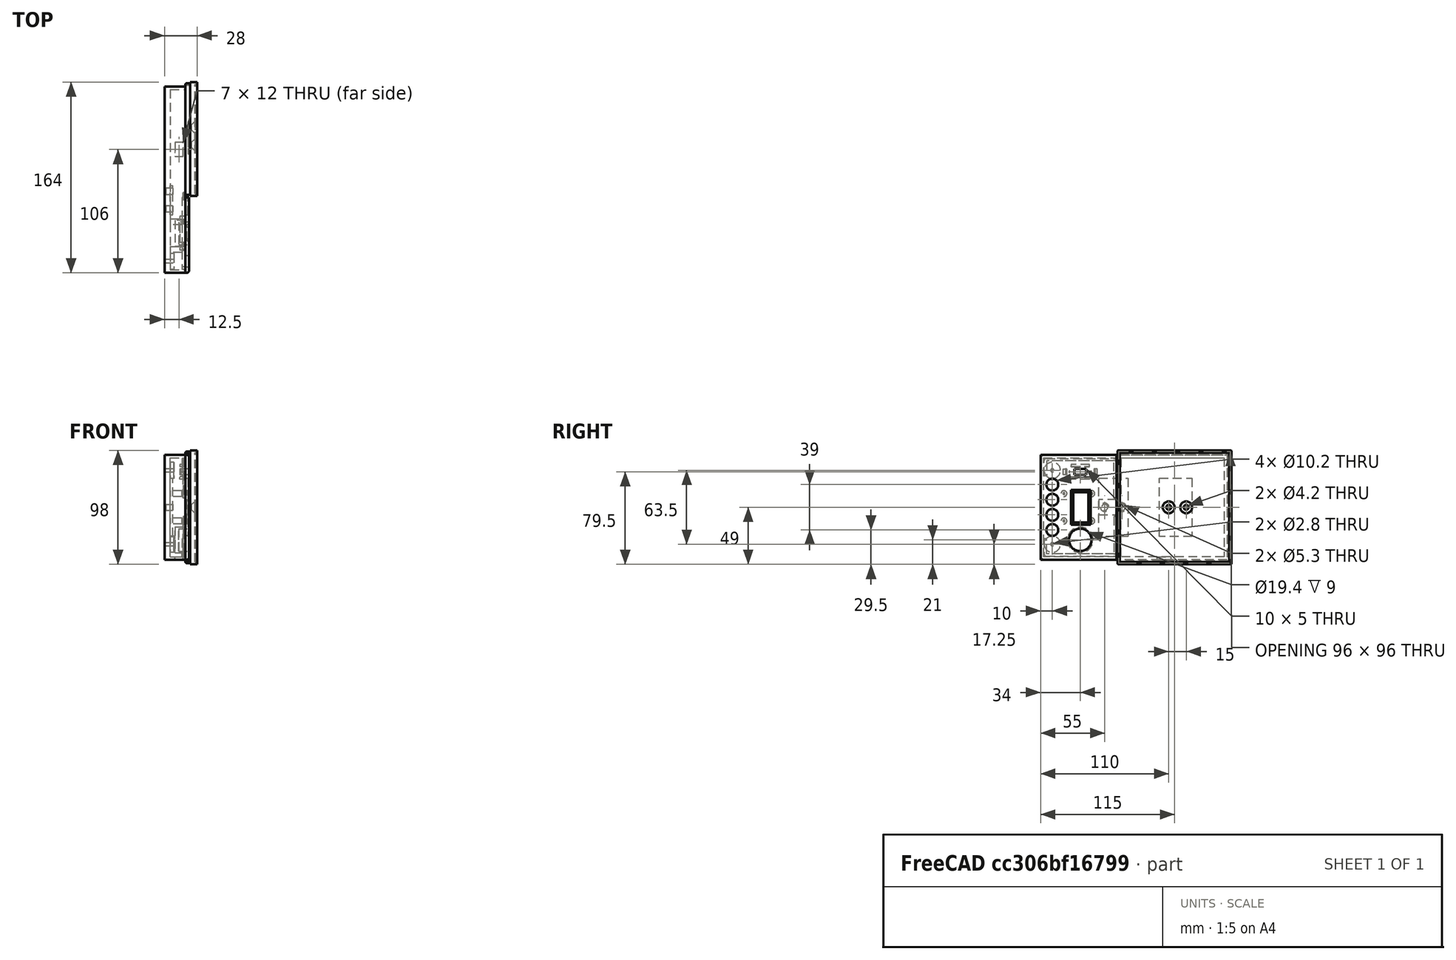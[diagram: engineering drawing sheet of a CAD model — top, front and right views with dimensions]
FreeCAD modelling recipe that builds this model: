
FCSTD DOCUMENT  (FreeCAD 0.19R24291 (Git))
Label: Waagenplattform
License: All rights reserved
LicenseURL: http://en.wikipedia.org/wiki/All_rights_reserved
objects: Sketcher::SketchObject×24, PartDesign::Fillet×18, PartDesign::Pad×16, PartDesign::Chamfer×16, PartDesign::Pocket×7, PartDesign::Body×3, Mesh::Feature×1
note: 141 computed .brp shape members not serialized (recipe doc carries the construction recipe); baked Part::Feature solids carry a one-line shape summary decoded from their .brp

FEATURE [Sketcher::SketchObject] Sketch
  FullyConstrained = true
  MapMode = 5
  Placement = pos=(0,0,0) rot=(0.57735,0.57735,0.57735;2.0944rad)
  Support = -> [YZ_Plane]
  sketch-geometry (4):
    g0: LineSegment StartX=0 StartY=45 StartZ=0 EndX=160 EndY=45 EndZ=0
    g1: LineSegment StartX=160 StartY=45 StartZ=0 EndX=160 EndY=-45 EndZ=0
    g2: LineSegment StartX=160 StartY=-45 StartZ=0 EndX=0 EndY=-45 EndZ=0
    g3: LineSegment StartX=0 StartY=-45 StartZ=0 EndX=0 EndY=45 EndZ=0
  constraints (12):
    c: Coincident(g0,g1)
    c: Coincident(g1,g2)
    c: Coincident(g2,g3)
    c: Coincident(g3,g0)
    c: Horizontal(g0)
    c: Horizontal(g2)
    c: Vertical(g1)
    c: Vertical(g3)
    c: DistanceX(g0,g0) = 160
    c: DistanceY(g3,g3) = 90
    c: PointOnObject(g-1,g3)
    c: Distance(g-1,g0) = 45
FEATURE [PartDesign::Pad] Pad
  Direction = (1,1,1)
  Length = 5
  Length2 = 100
  Placement = pos=(0,0,0) rot=(0.57735,0.57735,0.57735;2.0944rad)
  Profile = -> Sketch
  Refine = true
  Type = 0
FEATURE [Sketcher::SketchObject] Sketch001
  FullyConstrained = true
  MapMode = 5
  Placement = pos=(5,-1.1e-15,1.1e-15) rot=(0.57735,0.57735,0.57735;2.0944rad)
  Support = -> [Pad]
  sketch-geometry (2):
    g0: Circle CenterX=10 CenterY=31.75 CenterZ=0 NormalX=0 NormalY=0 NormalZ=1 AngleXU=0 Radius=7
    g1: Circle CenterX=10 CenterY=-31.75 CenterZ=0 NormalX=0 NormalY=0 NormalZ=1 AngleXU=0 Radius=7
  constraints (5):
    c: Distance(g0,g1) = 63.5
    c: Symmetric(g0,g1,g-1)
    c: DistanceX(g-1,g0) = 10
    c: Radius(g0) = 7
    c: Radius(g1) = 7
FEATURE [PartDesign::Pad] Pad001
  BaseFeature = -> Pad
  Direction = (1,1,1)
  Length = 3
  Length2 = 100
  Placement = pos=(0,0,0) rot=(0.57735,0.57735,0.57735;2.0944rad)
  Profile = -> Sketch001
  Refine = true
  Type = 0
FEATURE [Sketcher::SketchObject] Sketch002
  FullyConstrained = true
  MapMode = 5
  Placement = pos=(5,-1.1e-15,1.1e-15) rot=(0.57735,0.57735,0.57735;2.0944rad)
  Support = -> [Pad001]
  sketch-geometry (4):
    g0: Circle CenterX=20 CenterY=11.75 CenterZ=0 NormalX=0 NormalY=0 NormalZ=1 AngleXU=0 Radius=2.5
    g1: Circle CenterX=44 CenterY=11.75 CenterZ=0 NormalX=0 NormalY=0 NormalZ=1 AngleXU=0 Radius=2.5
    g2: Circle CenterX=20 CenterY=-11.75 CenterZ=0 NormalX=0 NormalY=0 NormalZ=1 AngleXU=0 Radius=2.5
    g3: Circle CenterX=44 CenterY=-11.75 CenterZ=0 NormalX=0 NormalY=0 NormalZ=1 AngleXU=0 Radius=2.5
  constraints (11):
    c: DistanceX(g2,g3) = 24
    c: DistanceY(g3,g1) = 23.5
    c: Vertical(g0,g2)
    c: Horizontal(g0,g1)
    c: Horizontal(g2,g3)
    c: Radius(g0) = 2.5
    c: Radius(g1) = 2.5
    c: Radius(g3) = 2.5
    c: Radius(g2) = 2.5
    c: Symmetric(g1,g3,g-1)
    c: DistanceX(g-1,g0) = 20
FEATURE [PartDesign::Pad] Pad002
  BaseFeature = -> Pad001
  Direction = (1,1,1)
  Length = 10
  Length2 = 100
  Placement = pos=(0,0,0) rot=(0.57735,0.57735,0.57735;2.0944rad)
  Profile = -> Sketch002
  Refine = true
  Type = 0
FEATURE [Sketcher::SketchObject] Sketch003
  ExternalGeometry = -> [Pad002]
  FullyConstrained = true
  MapMode = 5
  Placement = pos=(15,-8.8e-15,9.3e-15) rot=(0.57735,0.57735,0.57735;2.0944rad)
  Support = -> [Pad002]
  sketch-geometry (4):
    g0: Circle CenterX=44 CenterY=11.75 CenterZ=0 NormalX=0 NormalY=0 NormalZ=1 AngleXU=0 Radius=0.8
    g1: Circle CenterX=20 CenterY=11.75 CenterZ=0 NormalX=0 NormalY=0 NormalZ=1 AngleXU=0 Radius=0.8
    g2: Circle CenterX=20 CenterY=-11.75 CenterZ=0 NormalX=0 NormalY=0 NormalZ=1 AngleXU=0 Radius=0.8
    g3: Circle CenterX=44 CenterY=-11.75 CenterZ=0 NormalX=0 NormalY=0 NormalZ=1 AngleXU=0 Radius=0.8
  constraints (8):
    c: Coincident(g0,g-3)
    c: Radius(g0) = 0.8
    c: Coincident(g1,g-4)
    c: Coincident(g2,g-5)
    c: Coincident(g3,g-6)
    c: Radius(g1) = 0.8
    c: Radius(g2) = 0.8
    c: Radius(g3) = 0.8
FEATURE [PartDesign::Pad] Pad003
  BaseFeature = -> Pad002
  Direction = (1,1,1)
  Length = 2.5
  Length2 = 100
  Placement = pos=(0,0,0) rot=(0.57735,0.57735,0.57735;2.0944rad)
  Profile = -> Sketch003
  Refine = true
  Type = 0
FEATURE [Sketcher::SketchObject] Sketch004
  ExternalGeometry = -> [Pad003]
  FullyConstrained = true
  MapMode = 5
  Placement = pos=(8,-4.1e-15,3.5e-15) rot=(0.57735,0.57735,0.57735;2.0944rad)
  Support = -> [Pad003]
  sketch-geometry (2):
    g0: Circle CenterX=10 CenterY=31.75 CenterZ=0 NormalX=0 NormalY=0 NormalZ=1 AngleXU=0 Radius=1.4
    g1: Circle CenterX=10 CenterY=-31.75 CenterZ=0 NormalX=0 NormalY=0 NormalZ=1 AngleXU=0 Radius=1.4
  constraints (4):
    c: Coincident(g0,g-3)
    c: Coincident(g1,g-4)
    c: Radius(g0) = 1.4
    c: Radius(g1) = 1.4
FEATURE [PartDesign::Pocket] Pocket
  BaseFeature = -> Pad003
  Length = 8
  Length2 = 100
  Placement = pos=(0,0,0) rot=(0.57735,0.57735,0.57735;2.0944rad)
  Profile = -> Sketch004
  Refine = true
  Type = 0
FEATURE [Sketcher::SketchObject] Sketch005
  FullyConstrained = true
  MapMode = 5
  Placement = pos=(5,-1.1e-15,1.1e-15) rot=(0.57735,0.57735,0.57735;2.0944rad)
  Support = -> [Pocket]
  sketch-geometry (4):
    g0: LineSegment StartX=50 StartY=25 StartZ=0 EndX=75 EndY=25 EndZ=0
    g1: LineSegment StartX=75 StartY=25 StartZ=0 EndX=75 EndY=-25 EndZ=0
    g2: LineSegment StartX=75 StartY=-25 StartZ=0 EndX=50 EndY=-25 EndZ=0
    g3: LineSegment StartX=50 StartY=-25 StartZ=0 EndX=50 EndY=25 EndZ=0
  constraints (11):
    c: Coincident(g0,g1)
    c: Coincident(g1,g2)
    c: Coincident(g2,g3)
    c: Coincident(g3,g0)
    c: Horizontal(g0)
    c: Horizontal(g2)
    c: Vertical(g1)
    c: DistanceX(g0,g0) = 25
    c: DistanceY(g3,g3) = 50
    c: Symmetric(g0,g2,g-1)
    c: DistanceX(g-1,g0) = 50
FEATURE [PartDesign::Pad] Pad004
  BaseFeature = -> Pocket
  Direction = (1,1,1)
  Length = 2
  Length2 = 100
  Placement = pos=(0,0,0) rot=(0.57735,0.57735,0.57735;2.0944rad)
  Profile = -> Sketch005
  Refine = true
  Type = 0
FEATURE [Sketcher::SketchObject] Sketch006
  ExternalGeometry = -> [Pad004]
  FullyConstrained = true
  MapMode = 5
  Placement = pos=(7,-9.2e-15,6.2e-15) rot=(0.57735,0.57735,0.57735;2.0944rad)
  Support = -> [Pad004]
  sketch-geometry (2):
    g0: Circle CenterX=55 CenterY=0 CenterZ=0 NormalX=0 NormalY=0 NormalZ=1 AngleXU=0 Radius=2.65
    g1: Circle CenterX=70 CenterY=0 CenterZ=0 NormalX=0 NormalY=0 NormalZ=1 AngleXU=0 Radius=2.65
  constraints (6):
    c: PointOnObject(g0,g-1)
    c: PointOnObject(g1,g-1)
    c: DistanceX(g0,g1) = 15
    c: Distance(g0,g-3) = 5
    c: Radius(g0) = 2.65
    c: Radius(g1) = 2.65
FEATURE [PartDesign::Pocket] Pocket001
  BaseFeature = -> Pad004
  Length = 7
  Length2 = 100
  Placement = pos=(0,0,0) rot=(0.57735,0.57735,0.57735;2.0944rad)
  Profile = -> Sketch006
  Refine = true
  Type = 0
FEATURE [PartDesign::Chamfer] Chamfer
  Angle = 45
  Base = -> Pocket001 [Edge13]
  BaseFeature = -> Pocket001
  ChamferType = 0
  FlipDirection = false
  Placement = pos=(0,0,0) rot=(0.57735,0.57735,0.57735;2.0944rad)
  Refine = true
  Size = 1
  Size2 = 1
  SupportTransform = false
FEATURE [PartDesign::Chamfer] Chamfer001
  Angle = 45
  Base = -> Chamfer [Edge6]
  BaseFeature = -> Chamfer
  ChamferType = 0
  FlipDirection = false
  Placement = pos=(0,0,0) rot=(0.57735,0.57735,0.57735;2.0944rad)
  Refine = true
  Size = 1
  Size2 = 1
  SupportTransform = false
FEATURE [Sketcher::SketchObject] Sketch007
  ExternalGeometry = -> [Chamfer001]
  FullyConstrained = true
  MapMode = 5
  Placement = pos=(5,-1.1e-15,1.1e-15) rot=(0.57735,0.57735,0.57735;2.0944rad)
  Support = -> [Chamfer001]
  sketch-geometry (8):
    g0: LineSegment StartX=4e-14 StartY=45 StartZ=0 EndX=160 EndY=45 EndZ=0
    g1: LineSegment StartX=160 StartY=45 StartZ=0 EndX=160 EndY=-45 EndZ=0
    g2: LineSegment StartX=160 StartY=-45 StartZ=0 EndX=2.84e-14 EndY=-45 EndZ=0
    g3: LineSegment StartX=4e-14 StartY=-45 StartZ=0 EndX=4e-14 EndY=45 EndZ=0
    g4: LineSegment StartX=2.5 StartY=42.5 StartZ=0 EndX=157.5 EndY=42.5 EndZ=0
    g5: LineSegment StartX=157.5 StartY=42.5 StartZ=0 EndX=157.5 EndY=-42.5 EndZ=0
    g6: LineSegment StartX=157.5 StartY=-42.5 StartZ=0 EndX=2.5 EndY=-42.5 EndZ=0
    g7: LineSegment StartX=2.5 StartY=-42.5 StartZ=0 EndX=2.5 EndY=42.5 EndZ=0
  constraints (22):
    c: Coincident(g0,g1)
    c: Coincident(g1,g2)
    c: Coincident(g2,g3)
    c: Coincident(g3,g0)
    c: Horizontal(g0)
    c: Horizontal(g2)
    c: Vertical(g1)
    c: Vertical(g3)
    c: Coincident(g0,g-6)
    c: Coincident(g1,g-5)
    c: Coincident(g4,g5)
    c: Coincident(g5,g6)
    c: Coincident(g6,g7)
    c: Coincident(g7,g4)
    c: Horizontal(g4)
    c: Horizontal(g6)
    c: Vertical(g5)
    c: Vertical(g7)
    c: Distance(g4,g0) = 2.5
    c: Distance(g4,g1) = 2.5
    c: Distance(g5,g2) = 2.5
    c: Distance(g6,g3) = 2.5
FEATURE [PartDesign::Pad] Pad005
  BaseFeature = -> Chamfer001
  Direction = (1,1,1)
  Length = 13
  Length2 = 100
  Placement = pos=(0,0,0) rot=(0.57735,0.57735,0.57735;2.0944rad)
  Profile = -> Sketch007
  Refine = true
  Type = 0
FEATURE [Sketcher::SketchObject] Sketch008
  ExternalGeometry = -> [Pad005]
  FullyConstrained = true
  MapMode = 5
  Placement = pos=(-1.332e-13,-1.93e-14,-45) rot=(0.707107,0.707107,0;3.14159rad)
  Support = -> [Pad005]
  sketch-geometry (4):
    g0: LineSegment StartX=100 StartY=16 StartZ=0 EndX=112 EndY=16 EndZ=0
    g1: LineSegment StartX=112 StartY=16 StartZ=0 EndX=112 EndY=9 EndZ=0
    g2: LineSegment StartX=112 StartY=9 StartZ=0 EndX=100 EndY=9 EndZ=0
    g3: LineSegment StartX=100 StartY=9 StartZ=0 EndX=100 EndY=16 EndZ=0
  constraints (12):
    c: Coincident(g0,g1)
    c: Coincident(g1,g2)
    c: Coincident(g2,g3)
    c: Coincident(g3,g0)
    c: Horizontal(g0)
    c: Horizontal(g2)
    c: Vertical(g1)
    c: Vertical(g3)
    c: DistanceX(g0,g0) = 12
    c: DistanceY(g1,g1) = 7
    c: Distance(g1,g-3) = 9
    c: Distance(g2,g-4) = 100
FEATURE [PartDesign::Pocket] Pocket002
  BaseFeature = -> Pad005
  Length = 5
  Length2 = 100
  Placement = pos=(0,0,0) rot=(0.57735,0.57735,0.57735;2.0944rad)
  Profile = -> Sketch008
  Refine = true
  Type = 0
FEATURE [PartDesign::Body] Body
  Group = -> [Sketch,Pad,Sketch001,Pad001,Sketch002,Pad002,Sketch003,Pad003,Sketch004,Pocket,Sketch005,Pad004,Sketch006,Pocket001,Chamfer,Chamfer001,Sketch007,Pad005,Sketch008,Pocket002]
  Origin = -> Origin
  Tip = -> Pocket002
FEATURE [Sketcher::SketchObject] Sketch009
  AttachmentOffset = pos=(0,0,22) rot=(0,0,1;0rad)
  FullyConstrained = true
  MapMode = 5
  Placement = pos=(22,-4.9e-15,4.9e-15) rot=(0.57735,0.57735,0.57735;2.0944rad)
  Support = -> [YZ_Plane001]
  sketch-geometry (4):
    g0: LineSegment StartX=66 StartY=49 StartZ=0 EndX=164 EndY=49 EndZ=0
    g1: LineSegment StartX=164 StartY=49 StartZ=0 EndX=164 EndY=-49 EndZ=0
    g2: LineSegment StartX=164 StartY=-49 StartZ=0 EndX=66 EndY=-49 EndZ=0
    g3: LineSegment StartX=66 StartY=-49 StartZ=0 EndX=66 EndY=49 EndZ=0
  constraints (11):
    c: Coincident(g0,g1)
    c: Coincident(g1,g2)
    c: Coincident(g2,g3)
    c: Coincident(g3,g0)
    c: Horizontal(g0)
    c: Horizontal(g2)
    c: Vertical(g3)
    c: DistanceY(g1,g1) = 98
    c: DistanceX(g0,g0) = 98
    c: Symmetric(g0,g1,g-1)
    c: DistanceX(g-1,g0) = 66
FEATURE [PartDesign::Pad] Pad006
  Direction = (1,1,1)
  Length = 4
  Length2 = 100
  Placement = pos=(0,0,0) rot=(0.57735,0.57735,0.57735;2.0944rad)
  Profile = -> Sketch009
  Refine = true
  Type = 0
FEATURE [Sketcher::SketchObject] Sketch010
  ExternalGeometry = -> [Pad006]
  FullyConstrained = true
  MapMode = 5
  Placement = pos=(22,-4.8e-15,4.8e-15) rot=(0.57735,0.57735,-0.57735;4.18879rad)
  Support = -> [Pad006]
  sketch-geometry (4):
    g0: LineSegment StartX=130 StartY=25 StartZ=0 EndX=102 EndY=25 EndZ=0
    g1: LineSegment StartX=102 StartY=25 StartZ=0 EndX=102 EndY=-25 EndZ=0
    g2: LineSegment StartX=102 StartY=-25 StartZ=0 EndX=130 EndY=-25 EndZ=0
    g3: LineSegment StartX=130 StartY=-25 StartZ=0 EndX=130 EndY=25 EndZ=0
  constraints (11):
    c: Coincident(g0,g1)
    c: Coincident(g1,g2)
    c: Coincident(g2,g3)
    c: Coincident(g3,g0)
    c: Horizontal(g0)
    c: Horizontal(g2)
    c: Vertical(g3)
    c: DistanceX(g0,g0) = 28
    c: DistanceY(g3,g3) = 50
    c: Symmetric(g0,g1,g-1)
    c: Distance(g0,g-3) = 34
FEATURE [PartDesign::Pad] Pad007
  BaseFeature = -> Pad006
  Direction = (1,1,1)
  Length = 2
  Length2 = 100
  Placement = pos=(0,0,0) rot=(0.57735,0.57735,0.57735;2.0944rad)
  Profile = -> Sketch010
  Refine = true
  Type = 0
FEATURE [Sketcher::SketchObject] Sketch011
  ExternalGeometry = -> [Pad007]
  FullyConstrained = true
  MapMode = 5
  Placement = pos=(20,-7.6e-15,5.6e-15) rot=(-0.57735,-0.57735,0.57735;2.0944rad)
  Support = -> [Pad007]
  sketch-geometry (2):
    g0: Circle CenterX=125 CenterY=0 CenterZ=0 NormalX=0 NormalY=0 NormalZ=1 AngleXU=0 Radius=2.1
    g1: Circle CenterX=110 CenterY=0 CenterZ=0 NormalX=0 NormalY=0 NormalZ=1 AngleXU=0 Radius=2.1
  constraints (6):
    c: PointOnObject(g0,g-1)
    c: PointOnObject(g1,g-1)
    c: Radius(g0) = 2.1
    c: Radius(g1) = 2.1
    c: DistanceX(g1,g0) = 15
    c: Distance(g0,g-3) = 5
FEATURE [PartDesign::Pocket] Pocket003
  BaseFeature = -> Pad007
  Length = 6
  Length2 = 100
  Placement = pos=(0,0,0) rot=(0.57735,0.57735,0.57735;2.0944rad)
  Profile = -> Sketch011
  Refine = true
  Type = 0
FEATURE [Sketcher::SketchObject] Sketch012
  ExternalGeometry = -> [Pocket003]
  FullyConstrained = true
  MapMode = 5
  Placement = pos=(22,-4.8e-15,4.8e-15) rot=(0.57735,0.57735,-0.57735;4.18879rad)
  Support = -> [Pocket003]
  sketch-geometry (8):
    g0: LineSegment StartX=163 StartY=48 StartZ=0 EndX=163 EndY=-48 EndZ=0
    g1: LineSegment StartX=163 StartY=-48 StartZ=0 EndX=67 EndY=-48 EndZ=0
    g2: LineSegment StartX=67 StartY=-46 StartZ=0 EndX=161 EndY=-46 EndZ=0
    g3: LineSegment StartX=161 StartY=-46 StartZ=0 EndX=161 EndY=46 EndZ=0
    g4: LineSegment StartX=67 StartY=-46 StartZ=0 EndX=67 EndY=-48 EndZ=0
    g5: LineSegment StartX=161 StartY=46 StartZ=0 EndX=67 EndY=46 EndZ=0
    g6: LineSegment StartX=67 StartY=46 StartZ=0 EndX=67 EndY=48 EndZ=0
    g7: LineSegment StartX=67 StartY=48 StartZ=0 EndX=163 EndY=48 EndZ=0
  constraints (23):
    c: Vertical(g0)
    c: Coincident(g0,g1)
    c: Horizontal(g1)
    c: Horizontal(g2)
    c: Coincident(g2,g3)
    c: Vertical(g3)
    c: DistanceY(g1,g2) = 2
    c: DistanceX(g3,g0) = 2
    c: Coincident(g4,g2)
    c: Coincident(g4,g1)
    c: Coincident(g5,g3)
    c: Horizontal(g5)
    c: Coincident(g6,g5)
    c: Coincident(g7,g6)
    c: Coincident(g7,g0)
    c: Horizontal(g7)
    c: Vertical(g6)
    c: Vertical(g4)
    c: DistanceY(g5,g6) = 2
    c: DistanceY(g2,g5) = 92
    c: Symmetric(g5,g2,g-1)
    c: Distance(g-7,g3) = 31
    c: DistanceX(g7,g7) = 96
FEATURE [PartDesign::Pad] Pad008
  BaseFeature = -> Pocket003
  Direction = (1,1,1)
  Length = 4
  Length2 = 100
  Placement = pos=(0,0,0) rot=(0.57735,0.57735,0.57735;2.0944rad)
  Profile = -> Sketch012
  Refine = true
  Type = 0
FEATURE [Sketcher::SketchObject] Sketch013
  ExternalGeometry = -> [Pad008]
  FullyConstrained = true
  MapMode = 5
  Placement = pos=(26,-5.7e-15,5.7e-15) rot=(0.57735,0.57735,0.57735;2.0944rad)
  Support = -> [Pad008]
  sketch-geometry (8):
    g0: LineSegment StartX=66 StartY=49 StartZ=0 EndX=164 EndY=49 EndZ=0
    g1: LineSegment StartX=164 StartY=49 StartZ=0 EndX=164 EndY=-49 EndZ=0
    g2: LineSegment StartX=164 StartY=-49 StartZ=0 EndX=66 EndY=-49 EndZ=0
    g3: LineSegment StartX=66 StartY=-49 StartZ=0 EndX=66 EndY=49 EndZ=0
    g4: LineSegment StartX=68 StartY=47 StartZ=0 EndX=162 EndY=47 EndZ=0
    g5: LineSegment StartX=162 StartY=47 StartZ=0 EndX=162 EndY=-47 EndZ=0
    g6: LineSegment StartX=162 StartY=-47 StartZ=0 EndX=68 EndY=-47 EndZ=0
    g7: LineSegment StartX=68 StartY=-47 StartZ=0 EndX=68 EndY=47 EndZ=0
  constraints (22):
    c: Coincident(g0,g1)
    c: Coincident(g1,g2)
    c: Coincident(g2,g3)
    c: Coincident(g3,g0)
    c: Horizontal(g0)
    c: Horizontal(g2)
    c: Vertical(g1)
    c: Vertical(g3)
    c: Coincident(g0,g-4)
    c: Coincident(g1,g-6)
    c: Coincident(g4,g5)
    c: Coincident(g5,g6)
    c: Coincident(g6,g7)
    c: Coincident(g7,g4)
    c: Horizontal(g4)
    c: Horizontal(g6)
    c: Vertical(g5)
    c: Vertical(g7)
    c: DistanceY(g4,g0) = 2
    c: DistanceY(g2,g6) = 2
    c: DistanceX(g0,g4) = 2
    c: DistanceX(g4,g0) = 2
FEATURE [PartDesign::Pad] Pad009
  BaseFeature = -> Pad008
  Direction = (1,1,1)
  Length = 2
  Length2 = 100
  Placement = pos=(0,0,0) rot=(0.57735,0.57735,0.57735;2.0944rad)
  Profile = -> Sketch013
  Refine = true
  Type = 0
FEATURE [PartDesign::Chamfer] Chamfer002
  Angle = 45
  Base = -> Pad009 [Edge18]
  BaseFeature = -> Pad009
  ChamferType = 0
  FlipDirection = false
  Placement = pos=(0,0,0) rot=(0.57735,0.57735,0.57735;2.0944rad)
  Refine = true
  Size = 3
  Size2 = 1
  SupportTransform = false
FEATURE [PartDesign::Chamfer] Chamfer003
  Angle = 45
  Base = -> Chamfer002 [Edge6]
  BaseFeature = -> Chamfer002
  ChamferType = 0
  FlipDirection = false
  Placement = pos=(0,0,0) rot=(0.57735,0.57735,0.57735;2.0944rad)
  Refine = true
  Size = 3
  Size2 = 1
  SupportTransform = false
FEATURE [PartDesign::Chamfer] Chamfer004
  Angle = 45
  Base = -> Chamfer003 [Edge15]
  BaseFeature = -> Chamfer003
  ChamferType = 0
  FlipDirection = false
  Placement = pos=(0,0,0) rot=(0.57735,0.57735,0.57735;2.0944rad)
  Refine = true
  Size = 1
  Size2 = 1
  SupportTransform = false
FEATURE [PartDesign::Chamfer] Chamfer005
  Angle = 45
  Base = -> Chamfer004 [Edge17]
  BaseFeature = -> Chamfer004
  ChamferType = 0
  FlipDirection = false
  Placement = pos=(0,0,0) rot=(0.57735,0.57735,0.57735;2.0944rad)
  Refine = true
  Size = 1
  Size2 = 1
  SupportTransform = false
FEATURE [PartDesign::Chamfer] Chamfer006
  Angle = 45
  Base = -> Chamfer005 [Edge5]
  BaseFeature = -> Chamfer005
  ChamferType = 0
  FlipDirection = false
  Placement = pos=(0,0,0) rot=(0.57735,0.57735,0.57735;2.0944rad)
  Refine = true
  Size = 1
  Size2 = 1
  SupportTransform = false
FEATURE [PartDesign::Chamfer] Chamfer007
  Angle = 45
  Base = -> Chamfer006 [Edge2]
  BaseFeature = -> Chamfer006
  ChamferType = 0
  FlipDirection = false
  Placement = pos=(0,0,0) rot=(0.57735,0.57735,0.57735;2.0944rad)
  Refine = true
  Size = 1
  Size2 = 1
  SupportTransform = false
FEATURE [PartDesign::Fillet] Fillet
  Base = -> Chamfer007 [Edge19]
  BaseFeature = -> Chamfer007
  Placement = pos=(0,0,0) rot=(0.57735,0.57735,0.57735;2.0944rad)
  Radius = 1
  Refine = true
  SupportTransform = false
FEATURE [PartDesign::Fillet] Fillet001
  Base = -> Fillet [Edge17]
  BaseFeature = -> Fillet
  Placement = pos=(0,0,0) rot=(0.57735,0.57735,0.57735;2.0944rad)
  Radius = 1
  Refine = true
  SupportTransform = false
FEATURE [PartDesign::Fillet] Fillet002
  Base = -> Fillet001 [Edge18]
  BaseFeature = -> Fillet001
  Placement = pos=(0,0,0) rot=(0.57735,0.57735,0.57735;2.0944rad)
  Radius = 1
  Refine = true
  SupportTransform = false
FEATURE [PartDesign::Fillet] Fillet003
  Base = -> Fillet002 [Edge19]
  BaseFeature = -> Fillet002
  Placement = pos=(0,0,0) rot=(0.57735,0.57735,0.57735;2.0944rad)
  Radius = 1
  Refine = true
  SupportTransform = false
FEATURE [PartDesign::Fillet] Fillet004
  Base = -> Fillet003 [Edge67]
  BaseFeature = -> Fillet003
  Placement = pos=(0,0,0) rot=(0.57735,0.57735,0.57735;2.0944rad)
  Radius = 1
  Refine = true
  SupportTransform = false
FEATURE [PartDesign::Fillet] Fillet005
  Base = -> Fillet004 [Edge29]
  BaseFeature = -> Fillet004
  Placement = pos=(0,0,0) rot=(0.57735,0.57735,0.57735;2.0944rad)
  Radius = 1
  Refine = true
  SupportTransform = false
FEATURE [PartDesign::Fillet] Fillet006
  Base = -> Fillet005 [Edge35]
  BaseFeature = -> Fillet005
  Placement = pos=(0,0,0) rot=(0.57735,0.57735,0.57735;2.0944rad)
  Radius = 1
  Refine = true
  SupportTransform = false
FEATURE [PartDesign::Fillet] Fillet007
  Base = -> Fillet006 [Edge33]
  BaseFeature = -> Fillet006
  Placement = pos=(0,0,0) rot=(0.57735,0.57735,0.57735;2.0944rad)
  Radius = 1
  Refine = true
  SupportTransform = false
FEATURE [PartDesign::Fillet] Fillet008
  Base = -> Fillet007 [Edge42]
  BaseFeature = -> Fillet007
  Placement = pos=(0,0,0) rot=(0.57735,0.57735,0.57735;2.0944rad)
  Radius = 1
  Refine = true
  SupportTransform = false
FEATURE [PartDesign::Body] Body001
  Group = -> [Sketch009,Pad006,Sketch010,Pad007,Sketch011,Pocket003,Sketch012,Pad008,Sketch013,Pad009,Chamfer002,Chamfer003,Chamfer004,Chamfer005,Chamfer006,Chamfer007,Fillet,Fillet001,Fillet002,Fillet003,Fillet004,Fillet005,Fillet006,Fillet007,Fillet008]
  Origin = -> Origin001
  Tip = -> Fillet008
FEATURE [Sketcher::SketchObject] Sketch014
  FullyConstrained = false
  MapMode = 5
  Placement = pos=(0,0,0) rot=(0.57735,0.57735,0.57735;2.0944rad)
  Support = -> [YZ_Plane002]
  sketch-geometry (13):
    g0: LineSegment StartX=0 StartY=45 StartZ=0 EndX=65 EndY=45 EndZ=0
    g1: LineSegment StartX=65 StartY=45 StartZ=0 EndX=65 EndY=-45 EndZ=0
    g2: LineSegment StartX=65 StartY=-45 StartZ=0 EndX=0 EndY=-45 EndZ=0
    g3: LineSegment StartX=0 StartY=-45 StartZ=0 EndX=0 EndY=45 EndZ=0
    g4: Circle CenterX=10 CenterY=19.5 CenterZ=0 NormalX=0 NormalY=0 NormalZ=1 AngleXU=0 Radius=5.1
    g5: Circle CenterX=10 CenterY=6.5 CenterZ=0 NormalX=0 NormalY=0 NormalZ=1 AngleXU=0 Radius=5.1
    g6: Circle CenterX=10 CenterY=-6.5 CenterZ=0 NormalX=0 NormalY=0 NormalZ=1 AngleXU=0 Radius=5.1
    g7: Circle CenterX=10 CenterY=-19.5 CenterZ=0 NormalX=0 NormalY=0 NormalZ=1 AngleXU=0 Radius=5.1
    g8: LineSegment StartX=10 StartY=32.9737 StartZ=0 EndX=10 EndY=-31.9287 EndZ=0
    g9: LineSegment StartX=28 StartY=13 StartZ=0 EndX=41 EndY=13 EndZ=0
    g10: LineSegment StartX=41 StartY=13 StartZ=0 EndX=41 EndY=-13 EndZ=0
    g11: LineSegment StartX=41 StartY=-13 StartZ=0 EndX=28 EndY=-13 EndZ=0
    g12: LineSegment StartX=28 StartY=-13 StartZ=0 EndX=28 EndY=13 EndZ=0
  constraints (35):
    c: Coincident(g0,g1)
    c: Coincident(g1,g2)
    c: Coincident(g2,g3)
    c: Coincident(g3,g0)
    c: Horizontal(g0)
    c: Horizontal(g2)
    c: Vertical(g1)
    c: DistanceY(g3,g3) = 90
    c: Symmetric(g0,g2,g-1)
    c: PointOnObject(g0,g-2)
    c: DistanceX(g0,g0) = 65
    c: Radius(g4) = 5.1
    c: Radius(g5) = 5.1
    c: Radius(g6) = 5.1
    c: Radius(g7) = 5.1
    c: DistanceY(g5,g4) = 13
    c: DistanceY(g6,g5) = 13
    c: DistanceY(g7,g6) = 13
    c: Vertical(g8)
    c: PointOnObject(g4,g8)
    c: PointOnObject(g5,g8)
    c: PointOnObject(g7,g8)
    c: Symmetric(g5,g6,g-1)
    c: Distance(g8,g3) = 10
    c: Coincident(g9,g10)
    c: Coincident(g10,g11)
    c: Coincident(g11,g12)
    c: Coincident(g12,g9)
    c: Horizontal(g9)
    c: Horizontal(g11)
    c: Vertical(g12)
    c: Distance(g9,g3) = 28
    c: DistanceX(g9,g9) = 13
    c: DistanceY(g10,g10) = 26
    c: Symmetric(g9,g10,g-1)
FEATURE [PartDesign::Pad] Pad010
  Direction = (1,1,1)
  Length = 3
  Length2 = 100
  Placement = pos=(0,0,0) rot=(0.57735,0.57735,0.57735;2.0944rad)
  Profile = -> Sketch014
  Refine = true
  Type = 0
FEATURE [Sketcher::SketchObject] Sketch015
  ExternalGeometry = -> [Pad010]
  FullyConstrained = true
  MapMode = 5
  Placement = pos=(1e-16,0,0) rot=(0.57735,0.57735,-0.57735;4.18879rad)
  Support = -> [Pad010]
  sketch-geometry (4):
    g0: LineSegment StartX=50 StartY=6.5 StartZ=0 EndX=65 EndY=6.5 EndZ=0
    g1: LineSegment StartX=65 StartY=6.5 StartZ=0 EndX=65 EndY=-6.5 EndZ=0
    g2: LineSegment StartX=65 StartY=-6.5 StartZ=0 EndX=50 EndY=-6.5 EndZ=0
    g3: LineSegment StartX=50 StartY=-6.5 StartZ=0 EndX=50 EndY=6.5 EndZ=0
  constraints (11):
    c: Coincident(g0,g1)
    c: Coincident(g1,g2)
    c: Coincident(g2,g3)
    c: Coincident(g3,g0)
    c: Horizontal(g0)
    c: Horizontal(g2)
    c: Vertical(g1)
    c: DistanceY(g3,g3) = 13
    c: Distance(g0,g-3) = 9
    c: PointOnObject(g0,g-4)
    c: Symmetric(g0,g2,g-1)
FEATURE [PartDesign::Pocket] Pocket004
  BaseFeature = -> Pad010
  Length = 2
  Length2 = 100
  Placement = pos=(0,0,0) rot=(0.57735,0.57735,0.57735;2.0944rad)
  Profile = -> Sketch015
  Refine = true
  Type = 0
FEATURE [Sketcher::SketchObject] Sketch016
  ExternalGeometry = -> [Pocket004]
  FullyConstrained = true
  MapMode = 5
  Placement = pos=(1e-16,0,0) rot=(0.57735,0.57735,-0.57735;4.18879rad)
  Support = -> [Pocket004]
  sketch-geometry (12):
    g0: LineSegment StartX=3 StartY=27 StartZ=0 EndX=3 EndY=42 EndZ=0
    g1: LineSegment StartX=3 StartY=42 StartZ=0 EndX=65 EndY=42 EndZ=0
    g2: LineSegment StartX=65 StartY=42 StartZ=0 EndX=65 EndY=40 EndZ=0
    g3: LineSegment StartX=65 StartY=40 StartZ=0 EndX=5 EndY=40 EndZ=0
    g4: LineSegment StartX=5 StartY=40 StartZ=0 EndX=5 EndY=27 EndZ=0
    g5: LineSegment StartX=5 StartY=27 StartZ=0 EndX=3 EndY=27 EndZ=0
    g6: LineSegment StartX=3 StartY=-27 StartZ=0 EndX=3 EndY=-42 EndZ=0
    g7: LineSegment StartX=3 StartY=-42 StartZ=0 EndX=65 EndY=-42 EndZ=0
    g8: LineSegment StartX=65 StartY=-42 StartZ=0 EndX=65 EndY=-40 EndZ=0
    g9: LineSegment StartX=65 StartY=-40 StartZ=0 EndX=5 EndY=-40 EndZ=0
    g10: LineSegment StartX=5 StartY=-40 StartZ=0 EndX=5 EndY=-27 EndZ=0
    g11: LineSegment StartX=5 StartY=-27 StartZ=0 EndX=3 EndY=-27 EndZ=0
  constraints (36):
    c: Vertical(g0)
    c: Coincident(g0,g1)
    c: PointOnObject(g1,g-5)
    c: Horizontal(g1)
    c: Coincident(g1,g2)
    c: PointOnObject(g2,g-5)
    c: Coincident(g2,g3)
    c: Horizontal(g3)
    c: Coincident(g3,g4)
    c: Vertical(g4)
    c: Coincident(g4,g5)
    c: Coincident(g5,g0)
    c: DistanceY(g3,g0) = 2
    c: DistanceX(g0,g3) = 2
    c: Horizontal(g5)
    c: DistanceY(g0,g-4) = 3
    c: DistanceX(g-4,g0) = 3
    c: DistanceY(g0,g0) = 15
    c: Coincident(g6,g7)
    c: Horizontal(g7)
    c: Coincident(g7,g8)
    c: Coincident(g8,g9)
    c: Horizontal(g9)
    c: Coincident(g9,g10)
    c: Coincident(g10,g11)
    c: Coincident(g11,g6)
    c: Horizontal(g11)
    c: Vertical(g6)
    c: Vertical(g10)
    c: PointOnObject(g8,g-7)
    c: PointOnObject(g7,g-7)
    c: DistanceX(g11,g11) = 2
    c: DistanceY(g8,g8) = 2
    c: Distance(g6,g-4) = 3
    c: Distance(g6,g-6) = 3
    c: DistanceY(g6,g6) = 15
FEATURE [PartDesign::Pad] Pad011
  BaseFeature = -> Pocket004
  Direction = (1,1,1)
  Length = 3
  Length2 = 100
  Placement = pos=(0,0,0) rot=(0.57735,0.57735,0.57735;2.0944rad)
  Profile = -> Sketch016
  Refine = true
  Type = 0
FEATURE [PartDesign::Fillet] Fillet009
  Base = -> Pad011 [Edge4]
  BaseFeature = -> Pad011
  Placement = pos=(0,0,0) rot=(0.57735,0.57735,0.57735;2.0944rad)
  Radius = 2
  Refine = true
  SupportTransform = false
FEATURE [PartDesign::Fillet] Fillet010
  Base = -> Fillet009 [Edge7]
  BaseFeature = -> Fillet009
  Placement = pos=(0,0,0) rot=(0.57735,0.57735,0.57735;2.0944rad)
  Radius = 2
  Refine = true
  SupportTransform = false
FEATURE [PartDesign::Fillet] Fillet011
  Base = -> Fillet010 [Edge52]
  BaseFeature = -> Fillet010
  Placement = pos=(0,0,0) rot=(0.57735,0.57735,0.57735;2.0944rad)
  Radius = 2
  Refine = true
  SupportTransform = false
FEATURE [PartDesign::Chamfer] Chamfer008
  Angle = 45
  Base = -> Fillet011 [Edge24]
  BaseFeature = -> Fillet011
  ChamferType = 0
  FlipDirection = false
  Placement = pos=(0,0,0) rot=(0.57735,0.57735,0.57735;2.0944rad)
  Refine = true
  Size = 2
  Size2 = 1
  SupportTransform = false
FEATURE [PartDesign::Chamfer] Chamfer009
  Angle = 45
  Base = -> Chamfer008 [Edge2]
  BaseFeature = -> Chamfer008
  ChamferType = 0
  FlipDirection = false
  Placement = pos=(0,0,0) rot=(0.57735,0.57735,0.57735;2.0944rad)
  Refine = true
  Size = 2
  Size2 = 1
  SupportTransform = false
FEATURE [PartDesign::Chamfer] Chamfer010
  Angle = 45
  Base = -> Chamfer009 [Edge3]
  BaseFeature = -> Chamfer009
  ChamferType = 0
  FlipDirection = false
  Placement = pos=(0,0,0) rot=(0.57735,0.57735,0.57735;2.0944rad)
  Refine = true
  Size = 2
  Size2 = 1
  SupportTransform = false
FEATURE [PartDesign::Chamfer] Chamfer011
  Angle = 45
  Base = -> Chamfer010 [Edge2]
  BaseFeature = -> Chamfer010
  ChamferType = 0
  FlipDirection = false
  Placement = pos=(0,0,0) rot=(0.57735,0.57735,0.57735;2.0944rad)
  Refine = true
  Size = 2
  Size2 = 1
  SupportTransform = false
FEATURE [PartDesign::Fillet] Fillet012
  Base = -> Chamfer011 [Edge51]
  BaseFeature = -> Chamfer011
  Placement = pos=(0,0,0) rot=(0.57735,0.57735,0.57735;2.0944rad)
  Radius = 1
  Refine = true
  SupportTransform = false
FEATURE [PartDesign::Fillet] Fillet013
  Base = -> Fillet012 [Edge43]
  BaseFeature = -> Fillet012
  Placement = pos=(0,0,0) rot=(0.57735,0.57735,0.57735;2.0944rad)
  Radius = 1
  Refine = true
  SupportTransform = false
FEATURE [PartDesign::Fillet] Fillet014
  Base = -> Fillet013 [Edge29]
  BaseFeature = -> Fillet013
  Placement = pos=(0,0,0) rot=(0.57735,0.57735,0.57735;2.0944rad)
  Radius = 1
  Refine = true
  SupportTransform = false
FEATURE [PartDesign::Fillet] Fillet015
  Base = -> Fillet014 [Edge30]
  BaseFeature = -> Fillet014
  Placement = pos=(0,0,0) rot=(0.57735,0.57735,0.57735;2.0944rad)
  Radius = 1
  Refine = true
  SupportTransform = false
FEATURE [PartDesign::Fillet] Fillet016
  Base = -> Fillet015 [Edge64]
  BaseFeature = -> Fillet015
  Placement = pos=(0,0,0) rot=(0.57735,0.57735,0.57735;2.0944rad)
  Radius = 2
  Refine = true
  SupportTransform = false
FEATURE [PartDesign::Fillet] Fillet017
  Base = -> Fillet016 [Edge70]
  BaseFeature = -> Fillet016
  Placement = pos=(0,0,0) rot=(0.57735,0.57735,0.57735;2.0944rad)
  Radius = 2
  Refine = true
  SupportTransform = false
FEATURE [Sketcher::SketchObject] Sketch017
  ExternalGeometry = -> [Fillet017]
  FullyConstrained = true
  MapMode = 5
  Placement = pos=(1e-16,0,0) rot=(0.57735,0.57735,-0.57735;4.18879rad)
  Support = -> [Fillet017]
  sketch-geometry (1):
    g0: Circle CenterX=34 CenterY=28 CenterZ=0 NormalX=0 NormalY=0 NormalZ=1 AngleXU=0 Radius=11
  constraints (3):
    c: Radius(g0) = 11
    c: Distance(g0,g-4) = 17
    c: Distance(g0,g-3) = 34
FEATURE [PartDesign::Pad] Pad012
  BaseFeature = -> Fillet017
  Direction = (1,1,1)
  Length = 9
  Length2 = 100
  Placement = pos=(0,0,0) rot=(0.57735,0.57735,0.57735;2.0944rad)
  Profile = -> Sketch017
  Refine = true
  Type = 0
FEATURE [Sketcher::SketchObject] Sketch018
  FullyConstrained = true
  MapMode = 5
  Placement = pos=(1e-16,0,0) rot=(0.57735,0.57735,-0.57735;4.18879rad)
  Support = -> [Pad012]
FEATURE [Sketcher::SketchObject] Sketch019
  ExternalGeometry = -> [Pad012]
  FullyConstrained = true
  MapMode = 5
  Placement = pos=(3,-7e-16,7e-16) rot=(0.57735,0.57735,0.57735;2.0944rad)
  Support = -> [Pad012]
  sketch-geometry (1):
    g0: Circle CenterX=34 CenterY=-28 CenterZ=0 NormalX=0 NormalY=0 NormalZ=1 AngleXU=0 Radius=9.7
  constraints (3):
    c: Radius(g0) = 9.7
    c: Distance(g0,g-3) = 17
    c: Distance(g0,g-4) = 34
FEATURE [PartDesign::Pocket] Pocket005
  BaseFeature = -> Pad012
  Length = 9
  Length2 = 100
  Placement = pos=(0,0,0) rot=(0.57735,0.57735,0.57735;2.0944rad)
  Profile = -> Sketch019
  Refine = true
  Type = 0
FEATURE [Sketcher::SketchObject] Sketch020
  ExternalGeometry = -> [Pocket005]
  FullyConstrained = true
  MapMode = 5
  Placement = pos=(3,-7e-16,7e-16) rot=(0.57735,0.57735,0.57735;2.0944rad)
  Support = -> [Pocket005]
  sketch-geometry (4):
    g0: LineSegment StartX=29 StartY=33 StartZ=0 EndX=39 EndY=33 EndZ=0
    g1: LineSegment StartX=39 StartY=33 StartZ=0 EndX=39 EndY=28 EndZ=0
    g2: LineSegment StartX=39 StartY=28 StartZ=0 EndX=29 EndY=28 EndZ=0
    g3: LineSegment StartX=29 StartY=28 StartZ=0 EndX=29 EndY=33 EndZ=0
  constraints (12):
    c: Coincident(g0,g1)
    c: Coincident(g1,g2)
    c: Coincident(g2,g3)
    c: Coincident(g3,g0)
    c: Horizontal(g0)
    c: Horizontal(g2)
    c: Vertical(g1)
    c: Vertical(g3)
    c: DistanceX(g0,g0) = 10
    c: DistanceY(g1,g1) = 5
    c: Distance(g0,g-3) = 12
    c: Distance(g0,g-4) = 29
FEATURE [PartDesign::Pocket] Pocket006
  BaseFeature = -> Pocket005
  Length = 3
  Length2 = 100
  Placement = pos=(0,0,0) rot=(0.57735,0.57735,0.57735;2.0944rad)
  Profile = -> Sketch020
  Refine = true
  Type = 0
FEATURE [Sketcher::SketchObject] Sketch021
  ExternalGeometry = -> [Pocket006]
  FullyConstrained = true
  MapMode = 5
  Placement = pos=(1e-16,0,0) rot=(0.57735,0.57735,-0.57735;4.18879rad)
  Support = -> [Pocket006]
  sketch-geometry (2):
    g0: Circle CenterX=43.25 CenterY=-30.5 CenterZ=0 NormalX=0 NormalY=0 NormalZ=1 AngleXU=0 Radius=0.5
    g1: Circle CenterX=24.75 CenterY=-30.5 CenterZ=0 NormalX=0 NormalY=0 NormalZ=1 AngleXU=0 Radius=0.5
  constraints (8):
    c: Radius(g0) = 0.5
    c: Radius(g1) = 0.5
    c: Horizontal(g1,g0)
    c: DistanceX(g1,g0) = 18.5
    c: DistanceX(g-5,g0) = 4.25
    c: DistanceY(g-3,g-3) = 5
    c: DistanceX(g-6,g-6) = 10
    c: DistanceY(g-6,g0) = 2.5
FEATURE [PartDesign::Pad] Pad013
  BaseFeature = -> Pocket006
  Direction = (1,1,1)
  Length = 3
  Length2 = 100
  Placement = pos=(0,0,0) rot=(0.57735,0.57735,0.57735;2.0944rad)
  Profile = -> Sketch021
  Refine = true
  Type = 0
FEATURE [Sketcher::SketchObject] Sketch022
  ExternalGeometry = -> [Pad013]
  FullyConstrained = true
  MapMode = 5
  Placement = pos=(1e-16,0,0) rot=(0.57735,0.57735,-0.57735;4.18879rad)
  Support = -> [Pad013]
  sketch-geometry (16):
    g0: LineSegment StartX=45.7 StartY=-28 StartZ=0 EndX=48.7 EndY=-28 EndZ=0
    g1: LineSegment StartX=48.7 StartY=-28 StartZ=0 EndX=48.7 EndY=-33 EndZ=0
    g2: LineSegment StartX=48.7 StartY=-33 StartZ=0 EndX=45.7 EndY=-33 EndZ=0
    g3: LineSegment StartX=45.7 StartY=-33 StartZ=0 EndX=45.7 EndY=-28 EndZ=0
    g4: LineSegment StartX=22.3 StartY=-28 StartZ=0 EndX=19.3 EndY=-28 EndZ=0
    g5: LineSegment StartX=19.3 StartY=-28 StartZ=0 EndX=19.3 EndY=-33 EndZ=0
    g6: LineSegment StartX=19.3 StartY=-33 StartZ=0 EndX=22.3 EndY=-33 EndZ=0
    g7: LineSegment StartX=22.3 StartY=-33 StartZ=0 EndX=22.3 EndY=-28 EndZ=0
    g8: LineSegment StartX=26 StartY=-26.2 StartZ=0 EndX=42 EndY=-26.2 EndZ=0
    g9: LineSegment StartX=42 StartY=-26.2 StartZ=0 EndX=42 EndY=-24.2 EndZ=0
    g10: LineSegment StartX=42 StartY=-24.2 StartZ=0 EndX=26 EndY=-24.2 EndZ=0
    g11: LineSegment StartX=26 StartY=-24.2 StartZ=0 EndX=26 EndY=-26.2 EndZ=0
    g12: LineSegment StartX=26 StartY=-34.8 StartZ=0 EndX=42 EndY=-34.8 EndZ=0
    g13: LineSegment StartX=42 StartY=-34.8 StartZ=0 EndX=42 EndY=-36.8 EndZ=0
    g14: LineSegment StartX=42 StartY=-36.8 StartZ=0 EndX=26 EndY=-36.8 EndZ=0
    g15: LineSegment StartX=26 StartY=-36.8 StartZ=0 EndX=26 EndY=-34.8 EndZ=0
  constraints (50):
    c: Coincident(g0,g1)
    c: Coincident(g1,g2)
    c: Coincident(g2,g3)
    c: Coincident(g3,g0)
    c: Horizontal(g0)
    c: Horizontal(g2)
    c: Vertical(g1)
    c: Vertical(g3)
    c: DistanceY(g1,g1) = 5
    c: DistanceX(g2,g2) = 3
    c: Coincident(g4,g5)
    c: Coincident(g5,g6)
    c: Coincident(g6,g7)
    c: Coincident(g7,g4)
    c: Horizontal(g4)
    c: Horizontal(g6)
    c: Vertical(g5)
    c: Vertical(g7)
    c: DistanceY(g5,g5) = 5
    c: DistanceX(g6,g6) = 3
    c: Horizontal(g4,g-5)
    c: Horizontal(g-6,g0)
    c: DistanceX(g4,g0) = 23.4
    c: DistanceX(g-6,g0) = 6.7
    c: Coincident(g8,g9)
    c: Coincident(g9,g10)
    c: Coincident(g10,g11)
    c: Coincident(g11,g8)
    c: Horizontal(g8)
    c: Horizontal(g10)
    c: Vertical(g9)
    c: Vertical(g11)
    c: DistanceX(g10,g10) = 16
    c: DistanceY(g9,g9) = 2
    c: Coincident(g12,g13)
    c: Coincident(g13,g14)
    c: Coincident(g14,g15)
    c: Coincident(g15,g12)
    c: Horizontal(g12)
    c: Horizontal(g14)
    c: Vertical(g13)
    c: Vertical(g15)
    c: DistanceX(g14,g14) = 16
    c: DistanceY(g13,g13) = 2
    c: DistanceY(g12,g8) = 8.6
    c: Vertical(g8,g12)
    c: DistanceY(g-5,g-5) = 5
    c: DistanceY(g-6,g8) = 1.8
    c: DistanceX(g-3,g-3) = 10
    c: DistanceX(g-6,g8) = 3
FEATURE [PartDesign::Pad] Pad014
  BaseFeature = -> Pad013
  Direction = (1,1,1)
  Length = 5
  Length2 = 100
  Placement = pos=(0,0,0) rot=(0.57735,0.57735,0.57735;2.0944rad)
  Profile = -> Sketch022
  Refine = true
  Type = 0
FEATURE [PartDesign::Chamfer] Chamfer012
  Angle = 45
  Base = -> Pad014 [Edge108]
  BaseFeature = -> Pad014
  ChamferType = 0
  FlipDirection = false
  Placement = pos=(0,0,0) rot=(0.57735,0.57735,0.57735;2.0944rad)
  Refine = true
  Size = 1
  Size2 = 1
  SupportTransform = false
FEATURE [PartDesign::Chamfer] Chamfer013
  Angle = 45
  Base = -> Chamfer012 [Edge137]
  BaseFeature = -> Chamfer012
  ChamferType = 0
  FlipDirection = false
  Placement = pos=(0,0,0) rot=(0.57735,0.57735,0.57735;2.0944rad)
  Refine = true
  Size = 0.5
  Size2 = 1
  SupportTransform = false
FEATURE [PartDesign::Chamfer] Chamfer014
  Angle = 45
  Base = -> Chamfer013 [Edge136]
  BaseFeature = -> Chamfer013
  ChamferType = 0
  FlipDirection = false
  Placement = pos=(0,0,0) rot=(0.57735,0.57735,0.57735;2.0944rad)
  Refine = true
  Size = 0.5
  Size2 = 1
  SupportTransform = false
FEATURE [PartDesign::Chamfer] Chamfer015
  Angle = 45
  Base = -> Chamfer014 [Edge166]
  BaseFeature = -> Chamfer014
  ChamferType = 0
  FlipDirection = false
  Placement = pos=(0,0,0) rot=(0.57735,0.57735,0.57735;2.0944rad)
  Refine = true
  Size = 1
  Size2 = 1
  SupportTransform = false
FEATURE [Sketcher::SketchObject] Sketch023
  ExternalGeometry = -> [Chamfer015]
  FullyConstrained = true
  MapMode = 5
  Placement = pos=(1e-16,0,0) rot=(0.57735,0.57735,-0.57735;4.18879rad)
  Support = -> [Chamfer015]
  sketch-geometry (8):
    g0: LineSegment StartX=63 StartY=42 StartZ=0 EndX=69 EndY=42 EndZ=0
    g1: LineSegment StartX=69 StartY=42 StartZ=0 EndX=69 EndY=8 EndZ=0
    g2: LineSegment StartX=69 StartY=8 StartZ=0 EndX=63 EndY=8 EndZ=0
    g3: LineSegment StartX=63 StartY=8 StartZ=0 EndX=63 EndY=42 EndZ=0
    g4: LineSegment StartX=63 StartY=-42 StartZ=0 EndX=69 EndY=-42 EndZ=0
    g5: LineSegment StartX=69 StartY=-42 StartZ=0 EndX=69 EndY=-8 EndZ=0
    g6: LineSegment StartX=69 StartY=-8 StartZ=0 EndX=63 EndY=-8 EndZ=0
    g7: LineSegment StartX=63 StartY=-8 StartZ=0 EndX=63 EndY=-42 EndZ=0
  constraints (24):
    c: Coincident(g0,g1)
    c: Coincident(g1,g2)
    c: Coincident(g2,g3)
    c: Coincident(g3,g0)
    c: Horizontal(g0)
    c: Horizontal(g2)
    c: Vertical(g1)
    c: Vertical(g3)
    c: PointOnObject(g0,g-5)
    c: DistanceX(g2,g2) = 6
    c: DistanceY(g1,g1) = 34
    c: DistanceX(g-5,g0) = 4
    c: Coincident(g4,g5)
    c: Coincident(g5,g6)
    c: Coincident(g6,g7)
    c: Coincident(g7,g4)
    c: Horizontal(g4)
    c: Horizontal(g6)
    c: Vertical(g5)
    c: Vertical(g7)
    c: PointOnObject(g4,g-6)
    c: DistanceY(g5,g5) = 34
    c: DistanceX(g6,g6) = 6
    c: DistanceX(g-6,g4) = 4
FEATURE [PartDesign::Pad] Pad015
  BaseFeature = -> Chamfer015
  Direction = (1,1,1)
  Length = 2
  Length2 = 100
  Placement = pos=(0,0,0) rot=(0.57735,0.57735,0.57735;2.0944rad)
  Profile = -> Sketch023
  Refine = true
  Type = 0
FEATURE [PartDesign::Body] Body002
  Group = -> [Sketch014,Pad010,Sketch015,Pocket004,Sketch016,Pad011,Fillet009,Fillet010,Fillet011,Chamfer008,Chamfer009,Chamfer010,Chamfer011,Fillet012,Fillet013,Fillet014,Fillet015,Fillet016,Fillet017,Sketch017,Pad012,Sketch018,Sketch019,Pocket005,Sketch020,Pocket006,Sketch021,Pad013,Sketch022,Pad014,Chamfer012,Chamfer013,Chamfer014,Chamfer015,Sketch023,Pad015]
  Origin = -> Origin002
  Placement = pos=(18,0,0) rot=(0,0,1;0rad)
  Tip = -> Pad015
FEATURE [Mesh::Feature] Mesh  label="Body002 (Meshed)"
